# Revit family: Lüftungsrohrschelle Doppio, M 8-M10, DN 180, Gummi
name_source: partatom
category: HLS-Bauteile
revit_build: Autodesk Revit 2018 (Build: 20190510_1515(x64)
units: mm (PartAtom-declared; Revit-internal decimal feet)

## family parameters
Arbeitsebenenbasiert = Ja
Beim Laden mit Abzugskörper schneiden = Nein
Bemaßung runder Anschluss = Durchmesser verwenden
Gemeinsam genutzt = Ja
Immer vertikal = Nein
Raumberechnungspunkt = Nein
Teiletyp = Normal

## types (1)
- Lüftungsrohrschelle Doppio, M8/M10, DN 180, Gummi
    A = 24 mm  [stored 0.0787402 ft]
    AB = 0 mm  [stored 0 ft]
    Anschluss = M8/M10
    Anschlußhöhe = 24 mm
    Artikelnummer = 0449180
    B = 216 mm
    Bauart = zweiteilig
    Baustoffklasse = B2
    Breite = 196 mm
    Breite Material = 20 mm
    D = 182 mm
    D0 = 191 mm  [stored 0.62664 ft]
    DF1 = 23 mm
    DF2 = 36 mm
    DN = 180 mm
    DS = 5 mm  [stored 0.0164042 ft]
    DVS = 6 mm  [stored 0.019685 ft]
    Dämmstärke = 5 mm  [stored 0.0164042 ft]
    EAN = 4250928410993
    Fabrikat = MEFA
    Farbe Schalldämmeinlage = Schwarz
    Firma = MEFA Befestigungs- und Montagesysteme GmbH
    Gesamthöhe Dämmung = 8 mm  [stored 0.0262467 ft]
    Gewicht = 0.25 kg
    Gewicht pro Bauteil = 0.25 kg
    H = 214 mm
    HGA = 17 mm  [stored 0.0557743 ft]
    Höhe = 214 mm
    Kurztext1 = Lüftungsschelle Doppio 20x1.5
    Kurztext2 = DN 180 M8/M10 TPE
    L1 = 0 mm  [stored 0 ft]
    MB = 20 mm  [stored 0.0656168 ft]
    MD = 2 mm  [stored 0.00656168 ft]
    Material = Stahl
    Material Schalldämmeinlage = TPE
    Materialmaße = 20x1,5 mm
    Materialname = S235
    Mengeneinheit = St
    Nennweite DN Rohr = 180 mm
    Oberflaeche = galvanisch verzinkt
    R = 96 mm  [stored 0.314961 ft]
    RM = 97 mm  [stored 0.318241 ft]
    Rohraußendurchmesser = 183 mm
    Rohraußendurchmesser Zoll = Zoll
    S = 205 mm
    Schalldämmeinlage = Gummi TPE
    Sicke = 1 mm  [stored 0.00328084 ft]
    Stärke Material = 2 mm  [stored 0.00656168 ft]
    Verschluss = mit Rastverschluss
    Verschluss-Schraube = M6
    Vorgabe-Ansicht = 1219 mm
    max. Höhe = 194 mm
    max. Rohraußendurchmesser = 0 mm  [stored 0 ft]
    max. Temperaturbeständigkeit = +100 °C
    max. zul. Last = 0.61 kN
    max. zul. Last horizontal = 0.00 kN
    max. zul. Last vertikal = 0.00 kN
    min. Rohraußendurchmesser = 0 mm  [stored 0 ft]
    vpe = 25

note: [stored X ft] marks values corroborated as IEEE doubles in the binary element streams (Revit-internal decimal feet)

## geometry (parser evidence)
native form markers: Sweep x9
no freeform markers — native parametric forms only
